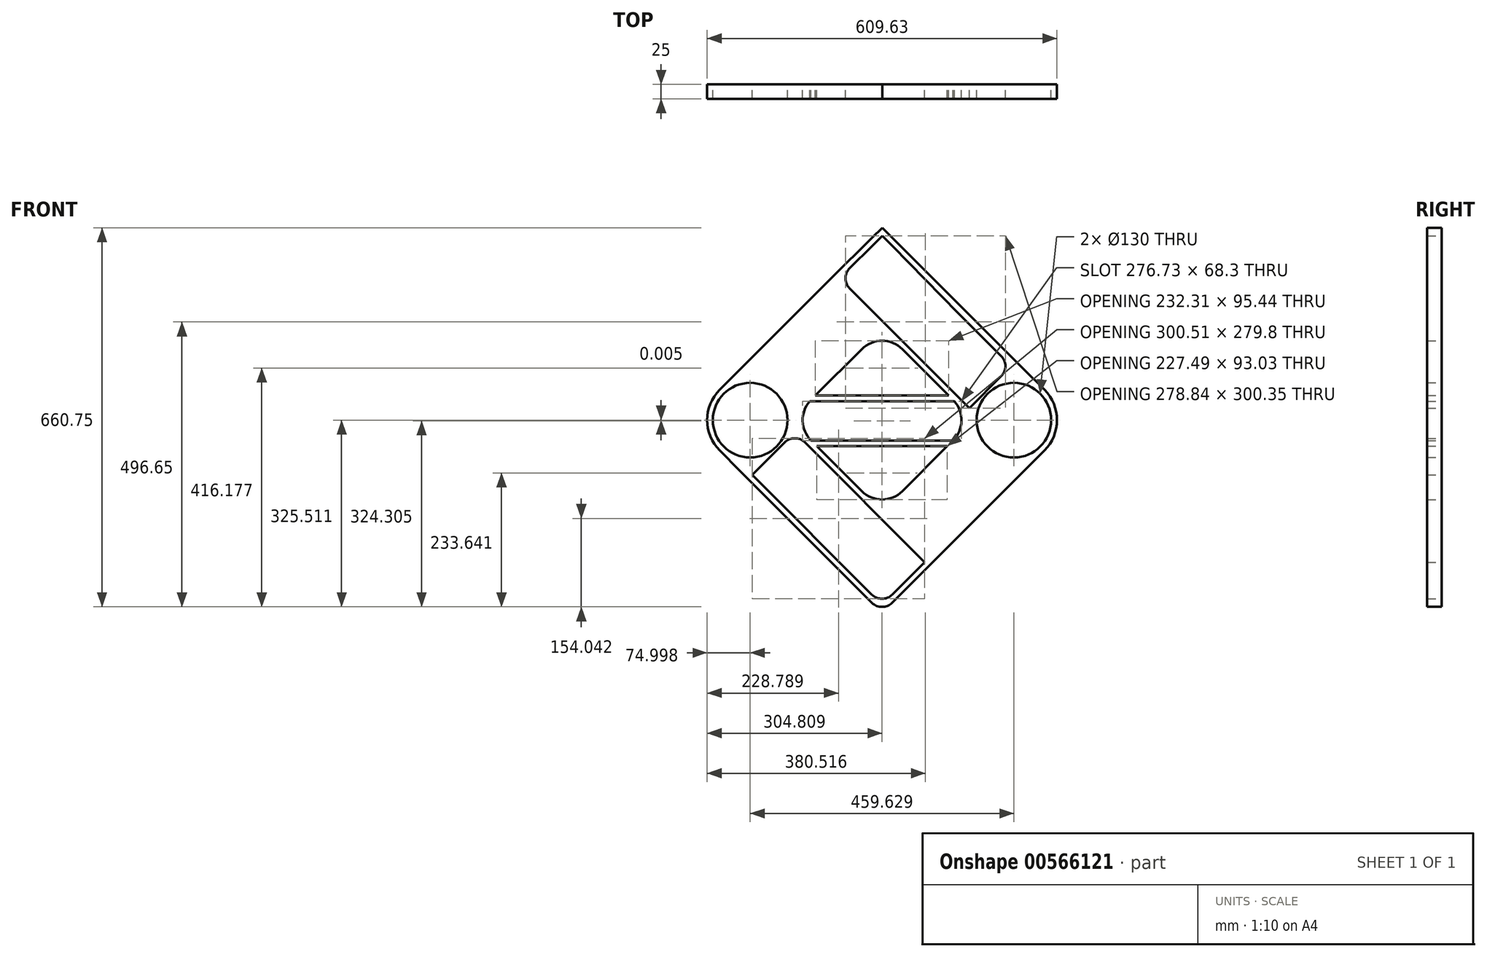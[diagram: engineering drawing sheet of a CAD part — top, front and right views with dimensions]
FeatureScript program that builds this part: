
annotation { "Feature Type Name" : "Feature", "Feature Type Description" : "" }
export const myFeature = defineFeature(function(context is Context, id is Id, definition is map)
    precondition{}
    {
        {
            var Q0;
            Q0=qCreatedBy(makeId("Front.planeOp"),FACE);
            var sketch = newSketch(context, id + "F0", { "sketchPlane" : qUnion([Q0])});
            skLineSegment(sketch, "E0", {"start": v(123.1, 36) * mm, "end": v(34.71, 124.4) * mm});
            skLineSegment(sketch, "E1", {"start": v(34.71, -123.1) * mm, "end": v(123.1, -34.7) * mm});
            skLineSegment(sketch, "E2", {"start": v(-116.8, 43.6) * mm, "end": v(-36, 124.4) * mm});
            skLineSegment(sketch, "E3", {"start": v(-124.39, -34.7) * mm, "end": v(-36, -123.1) * mm});
            skLineSegment(sketch, "E4", {"start": v(246.85, 89.05) * mm, "end": v(17.55, 318.34) * mm});
            skLineSegment(sketch, "E5", {"start": v(-17.68, 318.46) * mm, "end": v(-89.03, 248.14) * mm});
            skLineSegment(sketch, "E6", {"start": v(-89.03, 248.14) * mm, "end": v(-283.48, 53.68) * mm});
            skLineSegment(sketch, "E7", {"start": v(-283.49, -52.38) * mm, "end": v(-248.13, -87.74) * mm});
            skLineSegment(sketch, "E8", {"start": v(-248.13, -87.74) * mm, "end": v(-18.32, -317.54) * mm});
            skLineSegment(sketch, "E9", {"start": v(17.04, -317.54) * mm, "end": v(87.75, -246.83) * mm});
            skLineSegment(sketch, "E10", {"start": v(87.75, -246.83) * mm, "end": v(282.2, -52.38) * mm});
            skLineSegment(sketch, "E11", {"start": v(282.21, 53.69) * mm, "end": v(246.85, 89.05) * mm});
            skLineSegment(sketch, "E12.0", {"start": v(-17.73, 304.37) * mm, "end": v(-56.9, 265.76) * mm});
            skLineSegment(sketch, "E12.2", {"start": v(-57.03, 230.28) * mm, "end": v(6.43, 166.82) * mm});
            skLineSegment(sketch, "E12.3", {"start": v(151.64, 21.61) * mm, "end": v(6.43, 166.82) * mm});
            skLineSegment(sketch, "E13.0", {"start": v(17.04, -303.4) * mm, "end": v(73.6, -246.84) * mm});
            skLineSegment(sketch, "E13.1", {"start": v(-226.92, -94.8) * mm, "end": v(-18.32, -303.4) * mm});
            skLineSegment(sketch, "E13.4", {"start": v(-226.92, -94.8) * mm, "end": v(-170.35, -38.24) * mm});
            skPoint(sketch, "E14.visualSharp", {"position": v(-336.52, 335.88) * mm});
            skPoint(sketch, "E15.visualSharp", {"position": v(335.24, 0.65) * mm});
            skArc(sketch, "E15.filletArc", {"start": v(282.2, -52.38) * mm, "mid": v(304.18, 0.65) * mm, "end": v(282.21, 53.69) * mm});
            skPoint(sketch, "E16.visualSharp", {"position": v(321.1, 0.65) * mm});
            skArc(sketch, "E17.filletArc", {"start": v(-18.32, -303.4) * mm, "mid": v(-0.64, -310.72) * mm, "end": v(17.04, -303.4) * mm});
            skArc(sketch, "E18.filletArc", {"start": v(-18.32, -317.54) * mm, "mid": v(-0.64, -324.86) * mm, "end": v(17.04, -317.54) * mm});
            skArc(sketch, "E19.filletArc", {"start": v(-283.48, 53.68) * mm, "mid": v(-305.45, 0.65) * mm, "end": v(-283.49, -52.38) * mm});
            skPoint(sketch, "E20.visualSharp", {"position": v(-322.37, 0.65) * mm});
            skArc(sketch, "E21.filletArc", {"start": v(34.71, 124.4) * mm, "mid": v(-0.64, 139.04) * mm, "end": v(-36, 124.4) * mm});
            skPoint(sketch, "E22.visualSharp", {"position": v(-159.74, 0.65) * mm});
            skArc(sketch, "E22.filletArc", {"start": v(-126.64, 33.6) * mm, "mid": v(-139, -1) * mm, "end": v(-124.39, -34.7) * mm});
            skArc(sketch, "E23.filletArc", {"start": v(-36, -123.1) * mm, "mid": v(-0.64, -137.73) * mm, "end": v(34.71, -123.1) * mm});
            skPoint(sketch, "E24.visualSharp", {"position": v(158.46, 0.65) * mm});
            skArc(sketch, "E24.filletArc", {"start": v(123.1, -34.7) * mm, "mid": v(137.75, 0.65) * mm, "end": v(123.1, 36) * mm});
            skCircle(sketch, "E25", {"center": v(-59.3, -0.55) * mm, "radius": 14.15 * mm});
            skCircle(sketch, "E26", {"center": v(19.77, -0.55) * mm, "radius": 14.15 * mm});
            skCircle(sketch, "E27", {"center": v(59.31, -0.55) * mm, "radius": 14.15 * mm});
            skCircle(sketch, "E28", {"center": v(-19.77, -0.55) * mm, "radius": 14.15 * mm});
            skLineSegment(sketch, "E29", {"start": v(-124.39, -34.7) * mm, "end": v(123.1, -34.7) * mm});
            skLineSegment(sketch, "E30.0", {"start": v(-114.39, -44.7) * mm, "end": v(113.1, -44.7) * mm});
            skPoint(sketch, "E31.visualSharp", {"position": v(-152.67, -20.56) * mm});
            skLineSegment(sketch, "E31.filletArc", {"start": v(-152.67, -20.56) * mm, "end": v(-152.67, -20.56) * mm});
            skPoint(sketch, "E32.visualSharp", {"position": v(-226.92, -94.8) * mm});
            skLineSegment(sketch, "E32.filletArc", {"start": v(-226.92, -94.8) * mm, "end": v(-226.92, -94.8) * mm});
            skCircle(sketch, "E33", {"center": v(-230.45, 0.65) * mm, "radius": 65 * mm});
            skArc(sketch, "E34.filletArc", {"start": v(-135, -38.24) * mm, "mid": v(-152.67, -30.92) * mm, "end": v(-170.35, -38.24) * mm});
            skPoint(sketch, "E35.endSnap0", {"position": v(132.2, 203.7) * mm});
            skLineSegment(sketch, "E36", {"start": v(178.34, 48.31) * mm, "end": v(151.64, 21.61) * mm});
            skLineSegment(sketch, "E37", {"start": v(132.2, 187.44) * mm, "end": v(207.16, 112.5) * mm});
            skLineSegment(sketch, "E38", {"start": v(178.34, 48.31) * mm, "end": v(207.16, 77.14) * mm});
            skCircle(sketch, "E39", {"center": v(229.18, 0.66) * mm, "radius": 65 * mm});
            skLineSegment(sketch, "E40", {"start": v(17.5, 304.24) * mm, "end": v(132.2, 187.44) * mm});
            skLineSegment(sketch, "E41", {"start": v(-17.73, 304.37) * mm, "end": v(-0.13, 321.97) * mm});
            skLineSegment(sketch, "E42", {"start": v(-0.13, 321.97) * mm, "end": v(17.5, 304.24) * mm});
            skLineSegment(sketch, "E43", {"start": v(17.55, 318.34) * mm, "end": v(0, 335.89) * mm});
            skLineSegment(sketch, "E44", {"start": v(0, 335.89) * mm, "end": v(-17.68, 318.46) * mm});
            skPoint(sketch, "E45.visualSharp", {"position": v(-74.84, 248.08) * mm});
            skArc(sketch, "E45.filletArc", {"start": v(-56.9, 265.76) * mm, "mid": v(-64.35, 248.05) * mm, "end": v(-57.03, 230.28) * mm});
            skPoint(sketch, "E46.visualSharp", {"position": v(224.84, 94.81) * mm});
            skArc(sketch, "E46.filletArc", {"start": v(207.16, 77.14) * mm, "mid": v(214.48, 94.81) * mm, "end": v(207.16, 112.5) * mm});
            skLineSegment(sketch, "E47", {"start": v(-59.3, -0.55) * mm, "end": v(-59.3, 13.6) * mm});
            skLineSegment(sketch, "E48", {"start": v(-59.3, 13.6) * mm, "end": v(-59.3, 33.6) * mm});
            skLineSegment(sketch, "E49", {"start": v(-126.64, 33.6) * mm, "end": v(125.36, 33.6) * mm});
            skLineSegment(sketch, "E50.0", {"start": v(-116.8, 43.6) * mm, "end": v(115.52, 43.6) * mm});
            skLineSegment(sketch, "E51", {"start": v(-7.72, -165.52) * mm, "end": v(73.6, -246.84) * mm});
            skLineSegment(sketch, "E52", {"start": v(34.71, -123.1) * mm, "end": v(-7.72, -165.52) * mm});
            skLineSegment(sketch, "E53", {"start": v(-135, -38.24) * mm, "end": v(-7.72, -165.52) * mm});
            skLineSegment(sketch, "E54", {"start": v(32.94, -206.18) * mm, "end": v(188.82, -50.3) * mm});
            skLineSegment(sketch, "E55", {"start": v(110.88, -128.24) * mm, "end": v(135.25, -128.24) * mm});
            skSolve(sketch);
        }
        {
            var Q0;
            Q0 = qSketchRegion(id + "F0", true);
            var Q1;
            {var subQ9=sQuery(id+"F0.wireOp",EDGE,"E50.0");Q1=makeQuery(id+"F0.imprint","IMPRINT",FACE,{"disambiguationData":[TD([[makeQuery(id+"F0.imprint","IMPRINT",EDGE,{"derivedFrom":subQ9}),-1.0]])]});}
            var Q2;
            {var subQ0=sQuery(id+"F0.wireOp",EDGE,"E29");Q2=makeQuery(id+"F0.imprint","IMPRINT",FACE,{"disambiguationData":[TD([[makeQuery(id+"F0.imprint","IMPRINT",EDGE,{"derivedFrom":subQ0}),-1.0]])]});}
            extrude(context, id + "F1", {"entities" : qUnion([Q0, Q1, Q2]), "depth" : 25 * mm, "offsetDistance" : 25 * mm});
        }
    });
